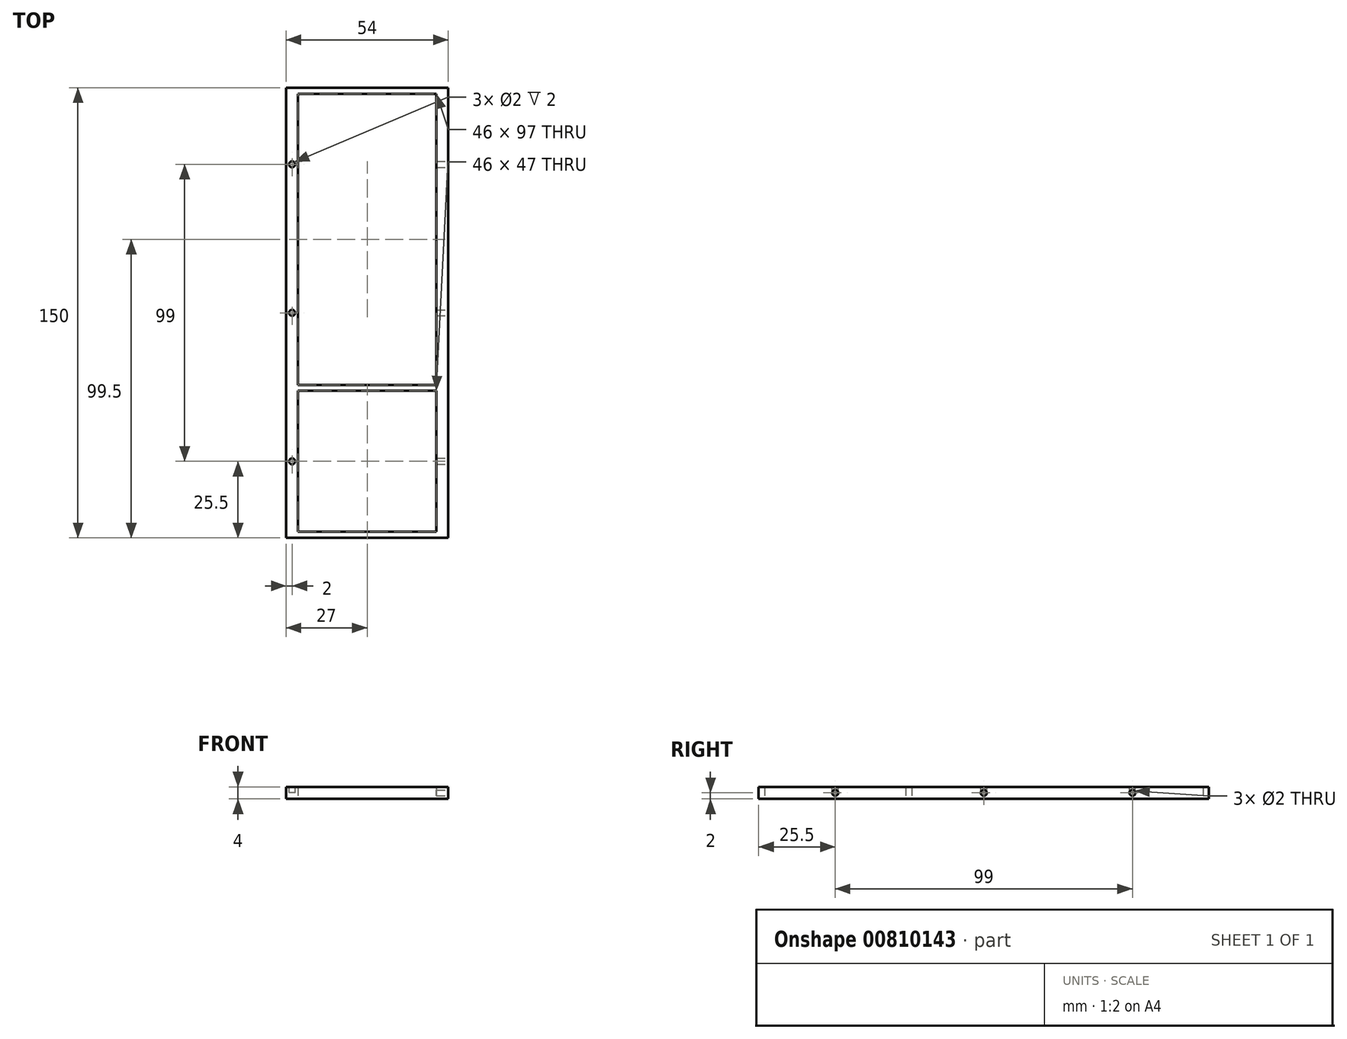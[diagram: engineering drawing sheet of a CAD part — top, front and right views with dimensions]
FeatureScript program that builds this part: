
annotation { "Feature Type Name" : "Feature", "Feature Type Description" : "" }
export const myFeature = defineFeature(function(context is Context, id is Id, definition is map)
    precondition{}
    {
        {
            var Q0;
            Q0=qCreatedBy(makeId("Top.planeOp"),FACE);
            var sketch = newSketch(context, id + "F0", { "sketchPlane" : qUnion([Q0])});
            skLineSegment(sketch, "E0.bottom", {"start": v(-27, 75) * mm, "end": v(27, 75) * mm});
            skLineSegment(sketch, "E0.top", {"start": v(-27, -75) * mm, "end": v(27, -75) * mm});
            skLineSegment(sketch, "E0.left", {"start": v(-27, 75) * mm, "end": v(-27, -75) * mm});
            skLineSegment(sketch, "E0.right", {"start": v(27, 75) * mm, "end": v(27, -75) * mm});
            skPoint(sketch, "E0.middle", {"position": v(0, 0) * mm});
            skLineSegment(sketch, "E1.bottom", {"start": v(-23, -26) * mm, "end": v(23, -26) * mm});
            skLineSegment(sketch, "E1.top", {"start": v(-23, -73) * mm, "end": v(23, -73) * mm});
            skLineSegment(sketch, "E1.left", {"start": v(-23, -26) * mm, "end": v(-23, -73) * mm});
            skLineSegment(sketch, "E1.right", {"start": v(23, -26) * mm, "end": v(23, -73) * mm});
            skPoint(sketch, "E1.middle", {"position": v(0, -49.5) * mm});
            skLineSegment(sketch, "E2.bottom", {"start": v(-23, 73) * mm, "end": v(23, 73) * mm});
            skLineSegment(sketch, "E2.top", {"start": v(-23, -24) * mm, "end": v(23, -24) * mm});
            skLineSegment(sketch, "E2.left", {"start": v(-23, 73) * mm, "end": v(-23, -24) * mm});
            skLineSegment(sketch, "E2.right", {"start": v(23, 73) * mm, "end": v(23, -24) * mm});
            skPoint(sketch, "E2.middle", {"position": v(0, 24.5) * mm});
            skSolve(sketch);
        }
        {
            var Q0;
            Q0 = qSketchRegion(id + "F0", true);
            extrude(context, id + "F1", {"entities" : qUnion([Q0]), "depth" : 4 * mm, "offsetDistance" : 25 * mm});
        }
        {
            var Q0;
            Q0=makeQuery(id+"F1.opExtrude","SWEPT_FACE",FACE,{"disambiguationData":[OSD([sQuery(id+"F0.wireOp",EDGE,"E0.right")])]});
            var sketch = newSketch(context, id + "F2", { "sketchPlane" : qUnion([Q0])});
            skPoint(sketch, "E3", {"position": v(-49.5, 2) * mm});
            skLineSegment(sketch, "E4", {"start": v(-24, 4) * mm, "end": v(-24, 0) * mm});
            skPoint(sketch, "E5", {"position": v(0, 2) * mm});
            skPoint(sketch, "E6", {"position": v(49.5, 2) * mm});
            skCircle(sketch, "E7", {"center": v(-49.5, 2) * mm, "radius": 1 * mm});
            skCircle(sketch, "E8", {"center": v(0, 2) * mm, "radius": 1 * mm});
            skCircle(sketch, "E9", {"center": v(49.5, 2) * mm, "radius": 1 * mm});
            skSolve(sketch);
        }
        {
            var Q0;
            Q0 = qSketchRegion(id + "F2", true);
            extrude(context, id + "F3", {"entities" : qUnion([Q0]), "operationType" : NewBodyOperationType.REMOVE, "oppositeDirection" : true, "depth" : 25 * mm, "offsetDistance" : 25 * mm});
        }
        {
            var Q0;
            Q0=makeQuery(id+"F1.opExtrude","CAP_FACE",FACE,{"disambiguationData":[OSD([sQuery(id+"F0.wireOp",EDGE,"E0.bottom"),sQuery(id+"F0.wireOp",EDGE,"E0.top"),sQuery(id+"F0.wireOp",EDGE,"E0.left"),sQuery(id+"F0.wireOp",EDGE,"E0.right"),sQuery(id+"F0.wireOp",EDGE,"E1.bottom"),sQuery(id+"F0.wireOp",EDGE,"E1.top"),sQuery(id+"F0.wireOp",EDGE,"E1.left"),sQuery(id+"F0.wireOp",EDGE,"E1.right"),sQuery(id+"F0.wireOp",EDGE,"E2.bottom"),sQuery(id+"F0.wireOp",EDGE,"E2.top"),sQuery(id+"F0.wireOp",EDGE,"E2.left"),sQuery(id+"F0.wireOp",EDGE,"E2.right")])],"isStart":false});
            var sketch = newSketch(context, id + "F4", { "sketchPlane" : qUnion([Q0])});
            skCircle(sketch, "E10", {"center": v(-25, -49.5) * mm, "radius": 1 * mm});
            skCircle(sketch, "E11", {"center": v(-25, 0) * mm, "radius": 1 * mm});
            skCircle(sketch, "E12", {"center": v(-25, 49.5) * mm, "radius": 1 * mm});
            skLineSegment(sketch, "E13", {"start": v(-23, -24) * mm, "end": v(-27, -24) * mm});
            skSolve(sketch);
        }
        {
            var Q0;
            Q0 = qSketchRegion(id + "F4", true);
            extrude(context, id + "F5", {"entities" : qUnion([Q0]), "operationType" : NewBodyOperationType.REMOVE, "oppositeDirection" : true, "depth" : 2 * mm, "offsetDistance" : 25 * mm});
        }
    });
